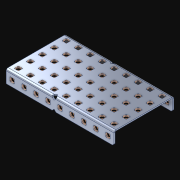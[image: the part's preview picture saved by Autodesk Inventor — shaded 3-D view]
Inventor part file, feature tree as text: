
AUTODESK INVENTOR PART (.ipt)
format: ipt  version: 2021 (Build 250183000, 183)  size: 1,618,944 bytes
history: native  units: in
note: dims shown in document units (in); Inventor stores cm internally (conversion verified against a paired STEP export)
features: extrude x64, other x64, sketch x4, pattern_linear x3
ambient origin geometry x8: Origin, YZ Plane, XZ Plane, XY Plane, X Axis, Y Axis, Z Axis, Center Point
bodies: Solid1 (feature_tree)
feature tree (135):
  pattern_linear  "Rectangular Pattern1"  Spacing1=0.182in  [1 undecoded]
  pattern_linear  "Rectangular Pattern2"  Spacing1=0.046in  [1 undecoded]
  pattern_linear  "Rectangular Pattern3"  Spacing1=0.5in  [1 undecoded]
  extrude  "Extrusion1"  Depth=0.046in
  sketch  "Sketch1"  dims[d0=0.182in]
  other  "Srf1"
  sketch  "Sketch2"  dims[d1=0.046in d2=0.0in]
  other  "Srf2"
  sketch  "Sketch3"  dims[d3=0.182in]
  other  "Srf3"
  other  "Srf4"
  other  "Srf5"
  other  "Srf6"
  other  "Srf7"
  other  "Srf8"
  other  "Srf9"
  other  "Srf10"
  other  "Srf11"
  other  "Srf38"
  other  "Srf39"
  other  "Srf40"
  other  "Srf41"
  other  "Srf42"
  other  "Srf43"
  other  "Srf44"
  other  "Srf45"
  other  "Srf72"
  other  "Srf73"
  other  "Srf74"
  other  "Srf75"
  other  "Srf76"
  other  "Srf77"
  other  "Srf78"
  other  "Srf79"
  other  "Srf80"
  other  "Srf107"
  other  "Srf108"
  other  "Srf109"
  other  "Srf110"
  other  "Srf111"
  other  "Srf112"
  other  "Srf113"
  other  "Srf114"
  other  "Srf115"
  other  "Srf142"
  other  "Srf143"
  other  "Srf144"
  other  "Srf145"
  other  "Srf146"
  other  "Srf147"
  other  "Srf148"
  other  "Srf149"
  other  "Srf150"
  other  "Srf177"
  other  "Srf178"
  other  "Srf179"
  other  "Srf180"
  other  "Srf181"
  other  "Srf182"
  other  "Srf183"
  other  "Srf184"
  other  "Srf185"
  other  "Srf212"
  other  "Srf213"
  other  "Srf214"
  other  "Srf215"
  other  "Srf216"
  other  "Srf217"
  other  "Srf218"
  other  "Srf219"
  sketch  "Sketch4"  dims[d4=0.046in d5=0.0in d6=0.182in d7=0.046in d8=0.0in d11=0.5in d12=3.5433in d14=0.5in d15=1.9685in d17=0.5in d18=3.5433in d20=0.5in d21=13.0in d22=0.0in]
  parser-record x1  (decoder bookkeeping rows leaked as tree rows — omitted from the tree; the rows remain in map.json)
  extrude  "ExtrusionSrf1"  Depth=0.046in
  extrude  "ExtrusionSrf2"  Depth=0.046in
  extrude  "ExtrusionSrf3"  Depth=0.046in
  extrude  "ExtrusionSrf4"  Depth=0.046in
  extrude  "ExtrusionSrf5"  Depth=0.046in
  extrude  "ExtrusionSrf6"  TaperAngle=0.0deg  [1 undecoded]
  extrude  "ExtrusionSrf7"  [1 undecoded]
  extrude  "ExtrusionSrf8"  [1 undecoded]
  extrude  "ExtrusionSrf9"  [1 undecoded]
  extrude  "ExtrusionSrf10"  [1 undecoded]
  extrude  "ExtrusionSrf11"  [1 undecoded]
  extrude  "ExtrusionSrf38"  [1 undecoded]
  extrude  "ExtrusionSrf39"  [1 undecoded]
  extrude  "ExtrusionSrf40"  [1 undecoded]
  extrude  "ExtrusionSrf41"  [1 undecoded]
  extrude  "ExtrusionSrf42"  [1 undecoded]
  extrude  "ExtrusionSrf43"  [1 undecoded]
  extrude  "ExtrusionSrf44"  [1 undecoded]
  extrude  "ExtrusionSrf45"  [1 undecoded]
  extrude  "ExtrusionSrf72"  [1 undecoded]
  extrude  "ExtrusionSrf73"  [1 undecoded]
  extrude  "ExtrusionSrf74"  [1 undecoded]
  extrude  "ExtrusionSrf75"  [1 undecoded]
  extrude  "ExtrusionSrf76"  [1 undecoded]
  extrude  "ExtrusionSrf77"  [1 undecoded]
  extrude  "ExtrusionSrf78"  [1 undecoded]
  extrude  "ExtrusionSrf79"  [1 undecoded]
  extrude  "ExtrusionSrf80"  [1 undecoded]
  extrude  "ExtrusionSrf107"  [1 undecoded]
  extrude  "ExtrusionSrf108"  [1 undecoded]
  extrude  "ExtrusionSrf109"  [1 undecoded]
  extrude  "ExtrusionSrf110"  [1 undecoded]
  extrude  "ExtrusionSrf111"  [1 undecoded]
  extrude  "ExtrusionSrf112"  [1 undecoded]
  extrude  "ExtrusionSrf113"  [1 undecoded]
  extrude  "ExtrusionSrf114"  [1 undecoded]
  extrude  "ExtrusionSrf115"  [1 undecoded]
  extrude  "ExtrusionSrf142"  [1 undecoded]
  extrude  "ExtrusionSrf143"  [1 undecoded]
  extrude  "ExtrusionSrf144"  [1 undecoded]
  extrude  "ExtrusionSrf145"  [1 undecoded]
  extrude  "ExtrusionSrf146"  [1 undecoded]
  extrude  "ExtrusionSrf147"  [1 undecoded]
  extrude  "ExtrusionSrf148"  [1 undecoded]
  extrude  "ExtrusionSrf149"  [1 undecoded]
  extrude  "ExtrusionSrf150"  [1 undecoded]
  extrude  "ExtrusionSrf177"  [1 undecoded]
  extrude  "ExtrusionSrf178"  [1 undecoded]
  extrude  "ExtrusionSrf179"  [1 undecoded]
  extrude  "ExtrusionSrf180"  [1 undecoded]
  extrude  "ExtrusionSrf181"  [1 undecoded]
  extrude  "ExtrusionSrf182"  [1 undecoded]
  extrude  "ExtrusionSrf183"  [1 undecoded]
  extrude  "ExtrusionSrf184"  [1 undecoded]
  extrude  "ExtrusionSrf185"  [1 undecoded]
  extrude  "ExtrusionSrf212"  [1 undecoded]
  extrude  "ExtrusionSrf213"  [1 undecoded]
  extrude  "ExtrusionSrf214"  [1 undecoded]
  extrude  "ExtrusionSrf215"  [1 undecoded]
  extrude  "ExtrusionSrf216"  [1 undecoded]
  extrude  "ExtrusionSrf217"  [1 undecoded]
  extrude  "ExtrusionSrf218"  [1 undecoded]
  extrude  "ExtrusionSrf219"  [1 undecoded]
note: 61 required parameter values undecoded (feature->parameter linkage not recoverable at this tier; creation-order binding heuristic only, values carry confidence <= 0.55)
